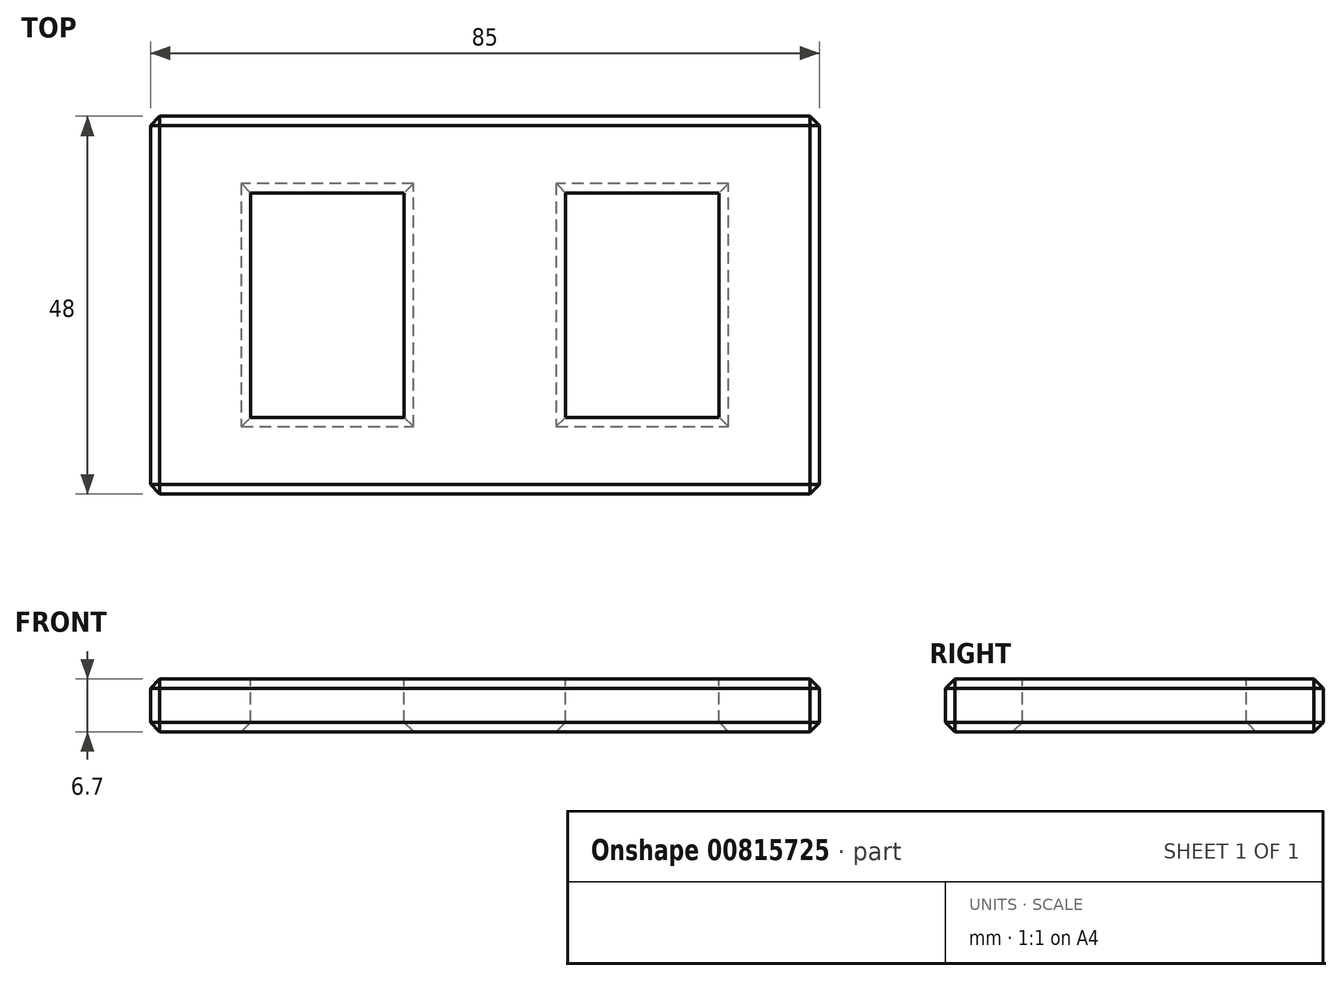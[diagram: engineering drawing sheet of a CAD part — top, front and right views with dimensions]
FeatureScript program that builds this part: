
annotation { "Feature Type Name" : "Feature", "Feature Type Description" : "" }
export const myFeature = defineFeature(function(context is Context, id is Id, definition is map)
    precondition{}
    {
        {
            var Q0;
            Q0=qCreatedBy(makeId("Top.planeOp"),FACE);
            var sketch = newSketch(context, id + "F0", { "sketchPlane" : qUnion([Q0])});
            skLineSegment(sketch, "E0.bottom", {"start": v(0, 24) * mm, "end": v(42.5, 24) * mm});
            skLineSegment(sketch, "E0.top", {"start": v(0, -24) * mm, "end": v(42.5, -24) * mm});
            skLineSegment(sketch, "E0.left", {"start": v(0, 24) * mm, "end": v(0, -24) * mm});
            skLineSegment(sketch, "E0.right", {"start": v(42.5, 24) * mm, "end": v(42.5, -24) * mm});
            skSolve(sketch);
        }
        {
            var Q0;
            Q0=makeQuery(id+"F0.imprint","IMPRINT",FACE,{"disambiguationData":[TD([[makeQuery(id+"F0.imprint","IMPRINT",EDGE,{"derivedFrom":sQuery(id+"F0.wireOp",EDGE,"E0.bottom")}),-1.0]])]});
            extrude(context, id + "F1", {"entities" : qUnion([Q0]), "depth" : 6.7 * mm, "offsetDistance" : 25 * mm});
        }
        {
            var Q0;
            Q0=makeQuery(id+"F1.opExtrude","CAP_FACE",FACE,{"disambiguationData":[OSD([sQuery(id+"F0.wireOp",EDGE,"E0.bottom"),sQuery(id+"F0.wireOp",EDGE,"E0.top"),sQuery(id+"F0.wireOp",EDGE,"E0.left"),sQuery(id+"F0.wireOp",EDGE,"E0.right")])],"isStart":false});
            var sketch = newSketch(context, id + "F2", { "sketchPlane" : qUnion([Q0])});
            skLineSegment(sketch, "E1.bottom", {"start": v(10.25, 14.25) * mm, "end": v(29.75, 14.25) * mm});
            skLineSegment(sketch, "E1.top", {"start": v(10.25, -14.25) * mm, "end": v(29.75, -14.25) * mm});
            skLineSegment(sketch, "E1.left", {"start": v(10.25, 14.25) * mm, "end": v(10.25, -14.25) * mm});
            skLineSegment(sketch, "E1.right", {"start": v(29.75, 14.25) * mm, "end": v(29.75, -14.25) * mm});
            skSolve(sketch);
        }
        {
            var Q0;
            Q0=makeQuery(id+"F2.imprint","IMPRINT",FACE,{"disambiguationData":[TD([[makeQuery(id+"F2.imprint","IMPRINT",EDGE,{"derivedFrom":sQuery(id+"F2.wireOp",EDGE,"E1.bottom")}),-1.0]])]});
            extrude(context, id + "F3", {"entities" : qUnion([Q0]), "operationType" : NewBodyOperationType.REMOVE, "oppositeDirection" : true, "depth" : 25 * mm, "offsetDistance" : 25 * mm});
        }
        {
            var Q0;
            Q0=makeQuery(id+"F1.opExtrude","SWEPT_BODY",BODY,{"disambiguationData":[OSD([sQuery(id+"F0.wireOp",EDGE,"E0.bottom"),sQuery(id+"F0.wireOp",EDGE,"E0.top"),sQuery(id+"F0.wireOp",EDGE,"E0.left"),sQuery(id+"F0.wireOp",EDGE,"E0.right")])]});
            var Q1;
            Q1=qCreatedBy(makeId("Right.planeOp"),FACE);
            mirror(context, id + "F4", {"operationType" : NewBodyOperationType.ADD, "entities" : qUnion([Q0]), "mirrorPlane" : qUnion([Q1])});
        }
        {
            var Q0;
            {var subQ0=makeQuery(id+"F1.opExtrude","CAP_EDGE",EDGE,{"disambiguationData":[OSD([sQuery(id+"F0.wireOp",EDGE,"E0.bottom")])],"isStart":false});Q0=makeQuery(id+"F4.boolean.opBoolean","MERGE",EDGE,{"derivedFrom":[subQ0,makeQuery(id+"F4.opPattern","COPY",EDGE,{"derivedFrom":subQ0,"instanceName":"1"})]});}
            var Q1;
            Q1=makeQuery(id+"F4.opPattern","COPY",EDGE,{"derivedFrom":makeQuery(id+"F1.opExtrude","CAP_EDGE",EDGE,{"disambiguationData":[OSD([sQuery(id+"F0.wireOp",EDGE,"E0.right")])],"isStart":false}),"instanceName":"1"});
            var Q2;
            {var subQ0=makeQuery(id+"F1.opExtrude","CAP_EDGE",EDGE,{"disambiguationData":[OSD([sQuery(id+"F0.wireOp",EDGE,"E0.top")])],"isStart":false});Q2=makeQuery(id+"F4.boolean.opBoolean","MERGE",EDGE,{"derivedFrom":[subQ0,makeQuery(id+"F4.opPattern","COPY",EDGE,{"derivedFrom":subQ0,"instanceName":"1"})]});}
            var Q3;
            Q3=makeQuery(id+"F1.opExtrude","CAP_EDGE",EDGE,{"disambiguationData":[OSD([sQuery(id+"F0.wireOp",EDGE,"E0.right")])],"isStart":true});
            var Q4;
            Q4=makeQuery(id+"F3.boolean.opBoolean","COPY",EDGE,{"derivedFrom":makeQuery(id+"F3.opExtrude","CAP_EDGE",EDGE,{"disambiguationData":[OSD([sQuery(id+"F2.wireOp",EDGE,"E1.right")])],"isStart":true})});
            var Q5;
            Q5=makeQuery(id+"F3.boolean.opBoolean","COPY",EDGE,{"derivedFrom":makeQuery(id+"F3.opExtrude","CAP_EDGE",EDGE,{"disambiguationData":[OSD([sQuery(id+"F2.wireOp",EDGE,"E1.left")])],"isStart":true})});
            var Q6;
            Q6=makeQuery(id+"F4.opPattern","COPY",EDGE,{"derivedFrom":makeQuery(id+"F3.boolean.opBoolean","COPY",EDGE,{"derivedFrom":makeQuery(id+"F3.opExtrude","CAP_EDGE",EDGE,{"disambiguationData":[OSD([sQuery(id+"F2.wireOp",EDGE,"E1.left")])],"isStart":true})}),"instanceName":"1"});
            var Q7;
            Q7=makeQuery(id+"F4.opPattern","COPY",EDGE,{"derivedFrom":makeQuery(id+"F3.boolean.opBoolean","COPY",EDGE,{"derivedFrom":makeQuery(id+"F3.opExtrude","CAP_EDGE",EDGE,{"disambiguationData":[OSD([sQuery(id+"F2.wireOp",EDGE,"E1.right")])],"isStart":true})}),"instanceName":"1"});
            var Q8;
            Q8=makeQuery(id+"F4.opPattern","COPY",EDGE,{"derivedFrom":makeQuery(id+"F3.boolean.opBoolean","COPY",EDGE,{"derivedFrom":makeQuery(id+"F3.opExtrude","CAP_EDGE",EDGE,{"disambiguationData":[OSD([sQuery(id+"F2.wireOp",EDGE,"E1.bottom")])],"isStart":true})}),"instanceName":"1"});
            var Q9;
            Q9=makeQuery(id+"F4.opPattern","COPY",EDGE,{"derivedFrom":makeQuery(id+"F3.boolean.opBoolean","COPY",EDGE,{"derivedFrom":makeQuery(id+"F3.opExtrude","CAP_EDGE",EDGE,{"disambiguationData":[OSD([sQuery(id+"F2.wireOp",EDGE,"E1.top")])],"isStart":true})}),"instanceName":"1"});
            var Q10;
            Q10=makeQuery(id+"F3.boolean.opBoolean","COPY",EDGE,{"derivedFrom":makeQuery(id+"F3.opExtrude","CAP_EDGE",EDGE,{"disambiguationData":[OSD([sQuery(id+"F2.wireOp",EDGE,"E1.top")])],"isStart":true})});
            var Q11;
            Q11=makeQuery(id+"F3.boolean.opBoolean","COPY",EDGE,{"derivedFrom":makeQuery(id+"F3.opExtrude","CAP_EDGE",EDGE,{"disambiguationData":[OSD([sQuery(id+"F2.wireOp",EDGE,"E1.bottom")])],"isStart":true})});
            var Q12;
            Q12=makeQuery(id+"F4.opPattern","COPY",EDGE,{"derivedFrom":makeQuery(id+"F1.opExtrude","SWEPT_EDGE",EDGE,{"disambiguationData":[OSD([sQuery(id+"F0.wireOp",EDGE,"E0.top"),sQuery(id+"F0.wireOp",EDGE,"E0.right")])]}),"instanceName":"1"});
            var Q13;
            Q13=makeQuery(id+"F4.opPattern","COPY",EDGE,{"derivedFrom":makeQuery(id+"F1.opExtrude","CAP_EDGE",EDGE,{"disambiguationData":[OSD([sQuery(id+"F0.wireOp",EDGE,"E0.right")])],"isStart":true}),"instanceName":"1"});
            var Q14;
            Q14=makeQuery(id+"F4.opPattern","COPY",EDGE,{"derivedFrom":makeQuery(id+"F1.opExtrude","SWEPT_EDGE",EDGE,{"disambiguationData":[OSD([sQuery(id+"F0.wireOp",EDGE,"E0.bottom"),sQuery(id+"F0.wireOp",EDGE,"E0.right")])]}),"instanceName":"1"});
            var Q15;
            {var subQ0=makeQuery(id+"F1.opExtrude","CAP_EDGE",EDGE,{"disambiguationData":[OSD([sQuery(id+"F0.wireOp",EDGE,"E0.top")])],"isStart":true});Q15=makeQuery(id+"F4.boolean.opBoolean","MERGE",EDGE,{"derivedFrom":[subQ0,makeQuery(id+"F4.opPattern","COPY",EDGE,{"derivedFrom":subQ0,"instanceName":"1"})]});}
            var Q16;
            Q16=makeQuery(id+"F4.opPattern","COPY",EDGE,{"derivedFrom":makeQuery(id+"F3.boolean.opBoolean","INTERSECT",EDGE,{"derivedFrom":[makeQuery(id+"F1.opExtrude","CAP_FACE",FACE,{"disambiguationData":[OSD([sQuery(id+"F0.wireOp",EDGE,"E0.bottom"),sQuery(id+"F0.wireOp",EDGE,"E0.top"),sQuery(id+"F0.wireOp",EDGE,"E0.left"),sQuery(id+"F0.wireOp",EDGE,"E0.right")])],"isStart":true}),makeQuery(id+"F3.opExtrude","SWEPT_FACE",FACE,{"disambiguationData":[OSD([sQuery(id+"F2.wireOp",EDGE,"E1.top")])]})]}),"instanceName":"1"});
            var Q17;
            Q17=makeQuery(id+"F4.opPattern","COPY",EDGE,{"derivedFrom":makeQuery(id+"F3.boolean.opBoolean","INTERSECT",EDGE,{"derivedFrom":[makeQuery(id+"F1.opExtrude","CAP_FACE",FACE,{"disambiguationData":[OSD([sQuery(id+"F0.wireOp",EDGE,"E0.bottom"),sQuery(id+"F0.wireOp",EDGE,"E0.top"),sQuery(id+"F0.wireOp",EDGE,"E0.left"),sQuery(id+"F0.wireOp",EDGE,"E0.right")])],"isStart":true}),makeQuery(id+"F3.opExtrude","SWEPT_FACE",FACE,{"disambiguationData":[OSD([sQuery(id+"F2.wireOp",EDGE,"E1.left")])]})]}),"instanceName":"1"});
            var Q18;
            Q18=makeQuery(id+"F4.opPattern","COPY",EDGE,{"derivedFrom":makeQuery(id+"F3.boolean.opBoolean","INTERSECT",EDGE,{"derivedFrom":[makeQuery(id+"F1.opExtrude","CAP_FACE",FACE,{"disambiguationData":[OSD([sQuery(id+"F0.wireOp",EDGE,"E0.bottom"),sQuery(id+"F0.wireOp",EDGE,"E0.top"),sQuery(id+"F0.wireOp",EDGE,"E0.left"),sQuery(id+"F0.wireOp",EDGE,"E0.right")])],"isStart":true}),makeQuery(id+"F3.opExtrude","SWEPT_FACE",FACE,{"disambiguationData":[OSD([sQuery(id+"F2.wireOp",EDGE,"E1.bottom")])]})]}),"instanceName":"1"});
            var Q19;
            Q19=makeQuery(id+"F4.opPattern","COPY",EDGE,{"derivedFrom":makeQuery(id+"F3.boolean.opBoolean","INTERSECT",EDGE,{"derivedFrom":[makeQuery(id+"F1.opExtrude","CAP_FACE",FACE,{"disambiguationData":[OSD([sQuery(id+"F0.wireOp",EDGE,"E0.bottom"),sQuery(id+"F0.wireOp",EDGE,"E0.top"),sQuery(id+"F0.wireOp",EDGE,"E0.left"),sQuery(id+"F0.wireOp",EDGE,"E0.right")])],"isStart":true}),makeQuery(id+"F3.opExtrude","SWEPT_FACE",FACE,{"disambiguationData":[OSD([sQuery(id+"F2.wireOp",EDGE,"E1.right")])]})]}),"instanceName":"1"});
            var Q20;
            Q20=makeQuery(id+"F3.boolean.opBoolean","INTERSECT",EDGE,{"derivedFrom":[makeQuery(id+"F1.opExtrude","CAP_FACE",FACE,{"disambiguationData":[OSD([sQuery(id+"F0.wireOp",EDGE,"E0.bottom"),sQuery(id+"F0.wireOp",EDGE,"E0.top"),sQuery(id+"F0.wireOp",EDGE,"E0.left"),sQuery(id+"F0.wireOp",EDGE,"E0.right")])],"isStart":true}),makeQuery(id+"F3.opExtrude","SWEPT_FACE",FACE,{"disambiguationData":[OSD([sQuery(id+"F2.wireOp",EDGE,"E1.left")])]})]});
            var Q21;
            Q21=makeQuery(id+"F3.boolean.opBoolean","INTERSECT",EDGE,{"derivedFrom":[makeQuery(id+"F1.opExtrude","CAP_FACE",FACE,{"disambiguationData":[OSD([sQuery(id+"F0.wireOp",EDGE,"E0.bottom"),sQuery(id+"F0.wireOp",EDGE,"E0.top"),sQuery(id+"F0.wireOp",EDGE,"E0.left"),sQuery(id+"F0.wireOp",EDGE,"E0.right")])],"isStart":true}),makeQuery(id+"F3.opExtrude","SWEPT_FACE",FACE,{"disambiguationData":[OSD([sQuery(id+"F2.wireOp",EDGE,"E1.right")])]})]});
            var Q22;
            Q22=makeQuery(id+"F3.boolean.opBoolean","INTERSECT",EDGE,{"derivedFrom":[makeQuery(id+"F1.opExtrude","CAP_FACE",FACE,{"disambiguationData":[OSD([sQuery(id+"F0.wireOp",EDGE,"E0.bottom"),sQuery(id+"F0.wireOp",EDGE,"E0.top"),sQuery(id+"F0.wireOp",EDGE,"E0.left"),sQuery(id+"F0.wireOp",EDGE,"E0.right")])],"isStart":true}),makeQuery(id+"F3.opExtrude","SWEPT_FACE",FACE,{"disambiguationData":[OSD([sQuery(id+"F2.wireOp",EDGE,"E1.bottom")])]})]});
            var Q23;
            Q23=makeQuery(id+"F3.boolean.opBoolean","INTERSECT",EDGE,{"derivedFrom":[makeQuery(id+"F1.opExtrude","CAP_FACE",FACE,{"disambiguationData":[OSD([sQuery(id+"F0.wireOp",EDGE,"E0.bottom"),sQuery(id+"F0.wireOp",EDGE,"E0.top"),sQuery(id+"F0.wireOp",EDGE,"E0.left"),sQuery(id+"F0.wireOp",EDGE,"E0.right")])],"isStart":true}),makeQuery(id+"F3.opExtrude","SWEPT_FACE",FACE,{"disambiguationData":[OSD([sQuery(id+"F2.wireOp",EDGE,"E1.top")])]})]});
            var Q24;
            Q24=makeQuery(id+"F1.opExtrude","SWEPT_EDGE",EDGE,{"disambiguationData":[OSD([sQuery(id+"F0.wireOp",EDGE,"E0.bottom"),sQuery(id+"F0.wireOp",EDGE,"E0.right")])]});
            var Q25;
            Q25=makeQuery(id+"F1.opExtrude","SWEPT_EDGE",EDGE,{"disambiguationData":[OSD([sQuery(id+"F0.wireOp",EDGE,"E0.top"),sQuery(id+"F0.wireOp",EDGE,"E0.right")])]});
            var Q26;
            Q26=makeQuery(id+"F1.opExtrude","CAP_EDGE",EDGE,{"disambiguationData":[OSD([sQuery(id+"F0.wireOp",EDGE,"E0.right")])],"isStart":false});
            var Q27;
            {var subQ0=makeQuery(id+"F1.opExtrude","CAP_EDGE",EDGE,{"disambiguationData":[OSD([sQuery(id+"F0.wireOp",EDGE,"E0.bottom")])],"isStart":true});Q27=makeQuery(id+"F4.boolean.opBoolean","MERGE",EDGE,{"derivedFrom":[subQ0,makeQuery(id+"F4.opPattern","COPY",EDGE,{"derivedFrom":subQ0,"instanceName":"1"})]});}
            chamfer(context, id + "F5", {"entities" : qUnion([Q0, Q1, Q2, Q3, Q4, Q5, Q6, Q7, Q8, Q9, Q10, Q11, Q12, Q13, Q14, Q15, Q16, Q17, Q18, Q19, Q20, Q21, Q22, Q23, Q24, Q25, Q26, Q27]), "width" : 1.2 * mm, "tangentPropagation" : true});
        }
    });
